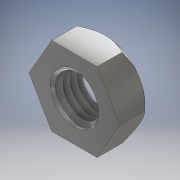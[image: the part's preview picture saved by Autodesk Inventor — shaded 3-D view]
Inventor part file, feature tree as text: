
AUTODESK INVENTOR PART (.ipt)
format: ipt  version: 2017 (Build 210142000, 142)  size: 379,392 bytes
history: native  units: mm
features: sketch x4, extrude x3, chamfer x1, plane x1, helix x1, fillet x1
ambient origin geometry x8: Origin, YZ Plane, XZ Plane, XY Plane, X Axis, Y Axis, Z Axis, Center Point
bodies: Solid1 (feature_tree)
feature tree (11):
  extrude  "Extrusion1"  Depth=7.5mm TaperAngle=0.0deg
  extrude  "Extrusion2"  Depth=7.5mm TaperAngle=45.0deg
  extrude  "Extrusion3"  Depth=7.5mm TaperAngle=0.0deg
  chamfer  "Chamfer1"  Distance=1.0mm Angle=45.0deg
  plane  "Work Plane1"
  helix  "Coil1"  [1 undecoded]
  fillet  "Fillet1"  Radius=1.7mm
  sketch  "Sketch1"  dims[d0=19.0mm d1=7.5mm d2=0.0mm]
  sketch  "Sketch2"  dims[d3=19.0mm d4=7.5mm d5=45.0deg]
  sketch  "Sketch3"  dims[d6=9.728mm d7=7.5mm d8=0.0mm d9=1.0mm d10=2.0mm d11=45.0deg d12=0.0mm d13=1.7mm]
  sketch  "Sketch4"  dims[d14=60.0deg d15=4.864mm d16=1.0mm d17=1.7mm d18=15.0mm d19=10.0mm d20=0.0mm d21=90.0deg d22=90.0deg d23=0.0mm d24=0.0mm d25=0.2mm]
note: 1 required parameter value undecoded (feature->parameter linkage not recoverable at this tier; creation-order binding heuristic only, values carry confidence <= 0.55)
